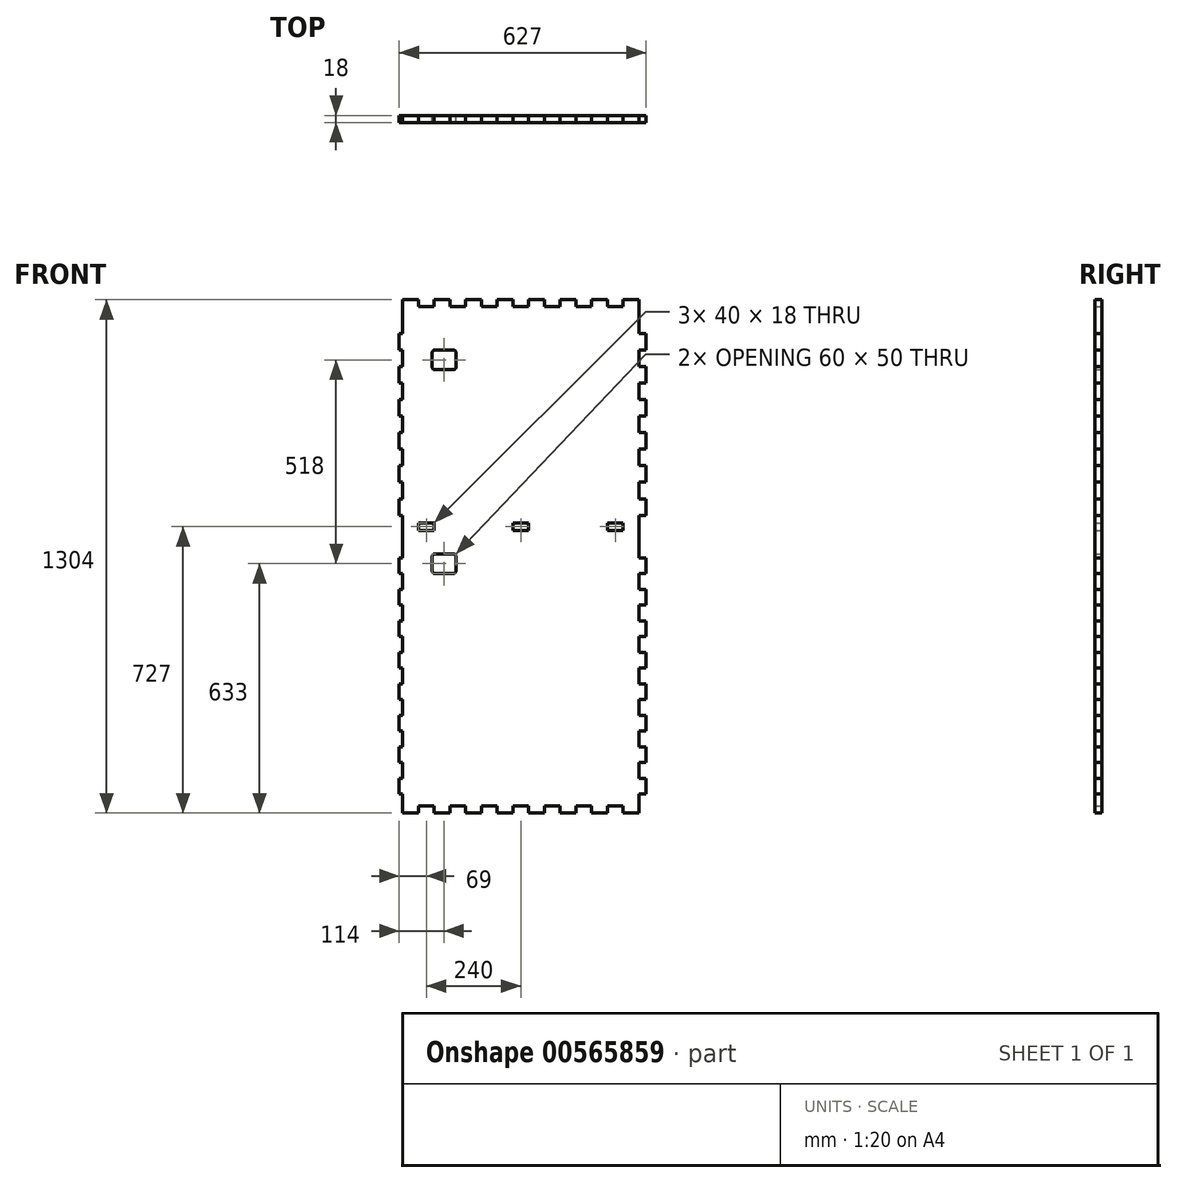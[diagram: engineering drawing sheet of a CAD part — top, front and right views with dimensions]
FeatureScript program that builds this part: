
annotation { "Feature Type Name" : "Feature", "Feature Type Description" : "" }
export const myFeature = defineFeature(function(context is Context, id is Id, definition is map)
    precondition{}
    {
        {
            var Q0;
            Q0=qCreatedBy(makeId("Front.planeOp"),FACE);
            var sketch = newSketch(context, id + "F0", { "sketchPlane" : qUnion([Q0])});
            skLineSegment(sketch, "E0", {"start": v(1332, 1218) * mm, "end": v(1332, 1304) * mm});
            skLineSegment(sketch, "E1", {"start": v(1332, 1304) * mm, "end": v(1292, 1304) * mm});
            skLineSegment(sketch, "E2", {"start": v(1292, 1304) * mm, "end": v(1292, 1286) * mm});
            skLineSegment(sketch, "E3", {"start": v(1292, 1286) * mm, "end": v(1252, 1286) * mm});
            skLineSegment(sketch, "E4", {"start": v(1252, 1304) * mm, "end": v(1252, 1286) * mm});
            skLineSegment(sketch, "E5", {"start": v(1252, 1304) * mm, "end": v(1212, 1304) * mm});
            skLineSegment(sketch, "E6", {"start": v(1212, 1304) * mm, "end": v(1212, 1286) * mm});
            skLineSegment(sketch, "E7", {"start": v(1212, 1286) * mm, "end": v(1172, 1286) * mm});
            skLineSegment(sketch, "E8", {"start": v(1172, 1304) * mm, "end": v(1172, 1286) * mm});
            skLineSegment(sketch, "E9", {"start": v(1172, 1304) * mm, "end": v(1132, 1304) * mm});
            skLineSegment(sketch, "E10", {"start": v(1132, 1304) * mm, "end": v(1132, 1286) * mm});
            skLineSegment(sketch, "E11", {"start": v(1132, 1286) * mm, "end": v(1092, 1286) * mm});
            skLineSegment(sketch, "E12", {"start": v(1092, 1304) * mm, "end": v(1092, 1286) * mm});
            skLineSegment(sketch, "E13", {"start": v(1092, 1304) * mm, "end": v(1052, 1304) * mm});
            skLineSegment(sketch, "E14", {"start": v(1052, 1304) * mm, "end": v(1052, 1286) * mm});
            skLineSegment(sketch, "E15", {"start": v(1052, 1286) * mm, "end": v(1012, 1286) * mm});
            skLineSegment(sketch, "E16", {"start": v(1012, 1304) * mm, "end": v(1012, 1286) * mm});
            skLineSegment(sketch, "E17", {"start": v(1012, 1304) * mm, "end": v(972, 1304) * mm});
            skLineSegment(sketch, "E18", {"start": v(972, 1304) * mm, "end": v(972, 1286) * mm});
            skLineSegment(sketch, "E19", {"start": v(972, 1286) * mm, "end": v(932, 1286) * mm});
            skLineSegment(sketch, "E20", {"start": v(932, 1304) * mm, "end": v(932, 1286) * mm});
            skLineSegment(sketch, "E21", {"start": v(932, 1304) * mm, "end": v(892, 1304) * mm});
            skLineSegment(sketch, "E22", {"start": v(892, 1304) * mm, "end": v(892, 1286) * mm});
            skLineSegment(sketch, "E23", {"start": v(892, 1286) * mm, "end": v(852, 1286) * mm});
            skLineSegment(sketch, "E24", {"start": v(852, 1304) * mm, "end": v(852, 1286) * mm});
            skLineSegment(sketch, "E25", {"start": v(852, 1304) * mm, "end": v(812, 1304) * mm});
            skLineSegment(sketch, "E26", {"start": v(812, 1304) * mm, "end": v(812, 1286) * mm});
            skLineSegment(sketch, "E27", {"start": v(812, 1286) * mm, "end": v(772, 1286) * mm});
            skLineSegment(sketch, "E28", {"start": v(772, 1304) * mm, "end": v(772, 1286) * mm});
            skLineSegment(sketch, "E29", {"start": v(772, 1304) * mm, "end": v(732, 1304) * mm});
            skLineSegment(sketch, "E30", {"start": v(732, 1218) * mm, "end": v(732, 1304) * mm});
            skLineSegment(sketch, "E31", {"start": v(723, 1218) * mm, "end": v(732, 1218) * mm});
            skLineSegment(sketch, "E32", {"start": v(723, 1176) * mm, "end": v(723, 1218) * mm});
            skLineSegment(sketch, "E33", {"start": v(723, 1176) * mm, "end": v(732, 1176) * mm});
            skLineSegment(sketch, "E34", {"start": v(732, 1134) * mm, "end": v(732, 1176) * mm});
            skLineSegment(sketch, "E35", {"start": v(723, 1134) * mm, "end": v(732, 1134) * mm});
            skLineSegment(sketch, "E36", {"start": v(723, 1092) * mm, "end": v(723, 1134) * mm});
            skLineSegment(sketch, "E37", {"start": v(723, 1092) * mm, "end": v(732, 1092) * mm});
            skLineSegment(sketch, "E38", {"start": v(732, 1050) * mm, "end": v(732, 1092) * mm});
            skLineSegment(sketch, "E39", {"start": v(723, 1050) * mm, "end": v(732, 1050) * mm});
            skLineSegment(sketch, "E40", {"start": v(723, 1008) * mm, "end": v(723, 1050) * mm});
            skLineSegment(sketch, "E41", {"start": v(723, 1008) * mm, "end": v(732, 1008) * mm});
            skLineSegment(sketch, "E42", {"start": v(732, 966) * mm, "end": v(732, 1008) * mm});
            skLineSegment(sketch, "E43", {"start": v(723, 966) * mm, "end": v(732, 966) * mm});
            skLineSegment(sketch, "E44", {"start": v(723, 924) * mm, "end": v(723, 966) * mm});
            skLineSegment(sketch, "E45", {"start": v(723, 924) * mm, "end": v(732, 924) * mm});
            skLineSegment(sketch, "E46", {"start": v(732, 882) * mm, "end": v(732, 924) * mm});
            skLineSegment(sketch, "E47", {"start": v(723, 882) * mm, "end": v(732, 882) * mm});
            skLineSegment(sketch, "E48", {"start": v(723, 840) * mm, "end": v(723, 882) * mm});
            skLineSegment(sketch, "E49", {"start": v(723, 840) * mm, "end": v(732, 840) * mm});
            skLineSegment(sketch, "E50", {"start": v(732, 798) * mm, "end": v(732, 840) * mm});
            skLineSegment(sketch, "E51", {"start": v(723, 798) * mm, "end": v(732, 798) * mm});
            skLineSegment(sketch, "E52", {"start": v(723, 756) * mm, "end": v(723, 798) * mm});
            skLineSegment(sketch, "E53", {"start": v(723, 756) * mm, "end": v(732, 756) * mm});
            skLineSegment(sketch, "E54", {"start": v(732, 648) * mm, "end": v(732, 756) * mm});
            skLineSegment(sketch, "E55", {"start": v(723, 648) * mm, "end": v(732, 648) * mm});
            skLineSegment(sketch, "E56", {"start": v(723, 608) * mm, "end": v(723, 648) * mm});
            skLineSegment(sketch, "E57", {"start": v(723, 608) * mm, "end": v(732, 608) * mm});
            skLineSegment(sketch, "E58", {"start": v(732, 568) * mm, "end": v(732, 608) * mm});
            skLineSegment(sketch, "E59", {"start": v(723, 568) * mm, "end": v(732, 568) * mm});
            skLineSegment(sketch, "E60", {"start": v(723, 528) * mm, "end": v(723, 568) * mm});
            skLineSegment(sketch, "E61", {"start": v(723, 528) * mm, "end": v(732, 528) * mm});
            skLineSegment(sketch, "E62", {"start": v(732, 488) * mm, "end": v(732, 528) * mm});
            skLineSegment(sketch, "E63", {"start": v(723, 488) * mm, "end": v(732, 488) * mm});
            skLineSegment(sketch, "E64", {"start": v(723, 448) * mm, "end": v(723, 488) * mm});
            skLineSegment(sketch, "E65", {"start": v(723, 448) * mm, "end": v(732, 448) * mm});
            skLineSegment(sketch, "E66", {"start": v(732, 408) * mm, "end": v(732, 448) * mm});
            skLineSegment(sketch, "E67", {"start": v(723, 408) * mm, "end": v(732, 408) * mm});
            skLineSegment(sketch, "E68", {"start": v(723, 368) * mm, "end": v(723, 408) * mm});
            skLineSegment(sketch, "E69", {"start": v(723, 368) * mm, "end": v(732, 368) * mm});
            skLineSegment(sketch, "E70", {"start": v(732, 328) * mm, "end": v(732, 368) * mm});
            skLineSegment(sketch, "E71", {"start": v(723, 328) * mm, "end": v(732, 328) * mm});
            skLineSegment(sketch, "E72", {"start": v(723, 288) * mm, "end": v(723, 328) * mm});
            skLineSegment(sketch, "E73", {"start": v(723, 288) * mm, "end": v(732, 288) * mm});
            skLineSegment(sketch, "E74", {"start": v(732, 248) * mm, "end": v(732, 288) * mm});
            skLineSegment(sketch, "E75", {"start": v(723, 248) * mm, "end": v(732, 248) * mm});
            skLineSegment(sketch, "E76", {"start": v(723, 208) * mm, "end": v(723, 248) * mm});
            skLineSegment(sketch, "E77", {"start": v(723, 208) * mm, "end": v(732, 208) * mm});
            skLineSegment(sketch, "E78", {"start": v(732, 168) * mm, "end": v(732, 208) * mm});
            skLineSegment(sketch, "E79", {"start": v(723, 168) * mm, "end": v(732, 168) * mm});
            skLineSegment(sketch, "E80", {"start": v(723, 128) * mm, "end": v(723, 168) * mm});
            skLineSegment(sketch, "E81", {"start": v(723, 128) * mm, "end": v(732, 128) * mm});
            skLineSegment(sketch, "E82", {"start": v(732, 88) * mm, "end": v(732, 128) * mm});
            skLineSegment(sketch, "E83", {"start": v(723, 88) * mm, "end": v(732, 88) * mm});
            skLineSegment(sketch, "E84", {"start": v(723, 48) * mm, "end": v(723, 88) * mm});
            skLineSegment(sketch, "E85", {"start": v(723, 48) * mm, "end": v(732, 48) * mm});
            skLineSegment(sketch, "E86", {"start": v(732, 0) * mm, "end": v(732, 48) * mm});
            skLineSegment(sketch, "E87", {"start": v(772, 0) * mm, "end": v(732, 0) * mm});
            skLineSegment(sketch, "E88", {"start": v(772, 18) * mm, "end": v(772, 0) * mm});
            skLineSegment(sketch, "E89", {"start": v(812, 18) * mm, "end": v(772, 18) * mm});
            skLineSegment(sketch, "E90", {"start": v(812, 18) * mm, "end": v(812, 0) * mm});
            skLineSegment(sketch, "E91", {"start": v(852, 0) * mm, "end": v(812, 0) * mm});
            skLineSegment(sketch, "E92", {"start": v(852, 18) * mm, "end": v(852, 0) * mm});
            skLineSegment(sketch, "E93", {"start": v(892, 18) * mm, "end": v(852, 18) * mm});
            skLineSegment(sketch, "E94", {"start": v(892, 18) * mm, "end": v(892, 0) * mm});
            skLineSegment(sketch, "E95", {"start": v(932, 0) * mm, "end": v(892, 0) * mm});
            skLineSegment(sketch, "E96", {"start": v(932, 18) * mm, "end": v(932, 0) * mm});
            skLineSegment(sketch, "E97", {"start": v(972, 18) * mm, "end": v(932, 18) * mm});
            skLineSegment(sketch, "E98", {"start": v(972, 18) * mm, "end": v(972, 0) * mm});
            skLineSegment(sketch, "E99", {"start": v(1012, 0) * mm, "end": v(972, 0) * mm});
            skLineSegment(sketch, "E100", {"start": v(1012, 18) * mm, "end": v(1012, 0) * mm});
            skLineSegment(sketch, "E101", {"start": v(1052, 18) * mm, "end": v(1012, 18) * mm});
            skLineSegment(sketch, "E102", {"start": v(1052, 18) * mm, "end": v(1052, 0) * mm});
            skLineSegment(sketch, "E103", {"start": v(1092, 0) * mm, "end": v(1052, 0) * mm});
            skLineSegment(sketch, "E104", {"start": v(1092, 18) * mm, "end": v(1092, 0) * mm});
            skLineSegment(sketch, "E105", {"start": v(1132, 18) * mm, "end": v(1092, 18) * mm});
            skLineSegment(sketch, "E106", {"start": v(1132, 18) * mm, "end": v(1132, 0) * mm});
            skLineSegment(sketch, "E107", {"start": v(1172, 0) * mm, "end": v(1132, 0) * mm});
            skLineSegment(sketch, "E108", {"start": v(1172, 18) * mm, "end": v(1172, 0) * mm});
            skLineSegment(sketch, "E109", {"start": v(1212, 18) * mm, "end": v(1172, 18) * mm});
            skLineSegment(sketch, "E110", {"start": v(1212, 18) * mm, "end": v(1212, 0) * mm});
            skLineSegment(sketch, "E111", {"start": v(1252, 0) * mm, "end": v(1212, 0) * mm});
            skLineSegment(sketch, "E112", {"start": v(1252, 18) * mm, "end": v(1252, 0) * mm});
            skLineSegment(sketch, "E113", {"start": v(1292, 18) * mm, "end": v(1252, 18) * mm});
            skLineSegment(sketch, "E114", {"start": v(1292, 18) * mm, "end": v(1292, 0) * mm});
            skLineSegment(sketch, "E115", {"start": v(1332, 0) * mm, "end": v(1292, 0) * mm});
            skLineSegment(sketch, "E116", {"start": v(1332, 0) * mm, "end": v(1332, 48) * mm});
            skLineSegment(sketch, "E117", {"start": v(1332, 48) * mm, "end": v(1350, 48) * mm});
            skLineSegment(sketch, "E118", {"start": v(1350, 48) * mm, "end": v(1350, 88) * mm});
            skLineSegment(sketch, "E119", {"start": v(1332, 88) * mm, "end": v(1350, 88) * mm});
            skLineSegment(sketch, "E120", {"start": v(1332, 88) * mm, "end": v(1332, 128) * mm});
            skLineSegment(sketch, "E121", {"start": v(1332, 128) * mm, "end": v(1350, 128) * mm});
            skLineSegment(sketch, "E122", {"start": v(1350, 128) * mm, "end": v(1350, 168) * mm});
            skLineSegment(sketch, "E123", {"start": v(1332, 168) * mm, "end": v(1350, 168) * mm});
            skLineSegment(sketch, "E124", {"start": v(1332, 168) * mm, "end": v(1332, 208) * mm});
            skLineSegment(sketch, "E125", {"start": v(1332, 208) * mm, "end": v(1350, 208) * mm});
            skLineSegment(sketch, "E126", {"start": v(1350, 208) * mm, "end": v(1350, 248) * mm});
            skLineSegment(sketch, "E127", {"start": v(1332, 248) * mm, "end": v(1350, 248) * mm});
            skLineSegment(sketch, "E128", {"start": v(1332, 248) * mm, "end": v(1332, 288) * mm});
            skLineSegment(sketch, "E129", {"start": v(1332, 288) * mm, "end": v(1350, 288) * mm});
            skLineSegment(sketch, "E130", {"start": v(1350, 288) * mm, "end": v(1350, 328) * mm});
            skLineSegment(sketch, "E131", {"start": v(1332, 328) * mm, "end": v(1350, 328) * mm});
            skLineSegment(sketch, "E132", {"start": v(1332, 328) * mm, "end": v(1332, 368) * mm});
            skLineSegment(sketch, "E133", {"start": v(1332, 368) * mm, "end": v(1350, 368) * mm});
            skLineSegment(sketch, "E134", {"start": v(1350, 368) * mm, "end": v(1350, 408) * mm});
            skLineSegment(sketch, "E135", {"start": v(1332, 408) * mm, "end": v(1350, 408) * mm});
            skLineSegment(sketch, "E136", {"start": v(1332, 408) * mm, "end": v(1332, 448) * mm});
            skLineSegment(sketch, "E137", {"start": v(1332, 448) * mm, "end": v(1350, 448) * mm});
            skLineSegment(sketch, "E138", {"start": v(1350, 448) * mm, "end": v(1350, 488) * mm});
            skLineSegment(sketch, "E139", {"start": v(1332, 488) * mm, "end": v(1350, 488) * mm});
            skLineSegment(sketch, "E140", {"start": v(1332, 488) * mm, "end": v(1332, 528) * mm});
            skLineSegment(sketch, "E141", {"start": v(1332, 528) * mm, "end": v(1350, 528) * mm});
            skLineSegment(sketch, "E142", {"start": v(1350, 528) * mm, "end": v(1350, 568) * mm});
            skLineSegment(sketch, "E143", {"start": v(1332, 568) * mm, "end": v(1350, 568) * mm});
            skLineSegment(sketch, "E144", {"start": v(1332, 568) * mm, "end": v(1332, 608) * mm});
            skLineSegment(sketch, "E145", {"start": v(1332, 608) * mm, "end": v(1350, 608) * mm});
            skLineSegment(sketch, "E146", {"start": v(1350, 608) * mm, "end": v(1350, 648) * mm});
            skLineSegment(sketch, "E147", {"start": v(1332, 648) * mm, "end": v(1350, 648) * mm});
            skLineSegment(sketch, "E148", {"start": v(1332, 648) * mm, "end": v(1332, 756) * mm});
            skLineSegment(sketch, "E149", {"start": v(1332, 756) * mm, "end": v(1350, 756) * mm});
            skLineSegment(sketch, "E150", {"start": v(1350, 756) * mm, "end": v(1350, 798) * mm});
            skLineSegment(sketch, "E151", {"start": v(1332, 798) * mm, "end": v(1350, 798) * mm});
            skLineSegment(sketch, "E152", {"start": v(1332, 798) * mm, "end": v(1332, 840) * mm});
            skLineSegment(sketch, "E153", {"start": v(1332, 840) * mm, "end": v(1350, 840) * mm});
            skLineSegment(sketch, "E154", {"start": v(1350, 840) * mm, "end": v(1350, 882) * mm});
            skLineSegment(sketch, "E155", {"start": v(1332, 882) * mm, "end": v(1350, 882) * mm});
            skLineSegment(sketch, "E156", {"start": v(1332, 882) * mm, "end": v(1332, 924) * mm});
            skLineSegment(sketch, "E157", {"start": v(1332, 924) * mm, "end": v(1350, 924) * mm});
            skLineSegment(sketch, "E158", {"start": v(1350, 924) * mm, "end": v(1350, 966) * mm});
            skLineSegment(sketch, "E159", {"start": v(1332, 966) * mm, "end": v(1350, 966) * mm});
            skLineSegment(sketch, "E160", {"start": v(1332, 966) * mm, "end": v(1332, 1008) * mm});
            skLineSegment(sketch, "E161", {"start": v(1332, 1008) * mm, "end": v(1350, 1008) * mm});
            skLineSegment(sketch, "E162", {"start": v(1350, 1008) * mm, "end": v(1350, 1050) * mm});
            skLineSegment(sketch, "E163", {"start": v(1332, 1050) * mm, "end": v(1350, 1050) * mm});
            skLineSegment(sketch, "E164", {"start": v(1332, 1050) * mm, "end": v(1332, 1092) * mm});
            skLineSegment(sketch, "E165", {"start": v(1332, 1092) * mm, "end": v(1350, 1092) * mm});
            skLineSegment(sketch, "E166", {"start": v(1350, 1092) * mm, "end": v(1350, 1134) * mm});
            skLineSegment(sketch, "E167", {"start": v(1332, 1134) * mm, "end": v(1350, 1134) * mm});
            skLineSegment(sketch, "E168", {"start": v(1332, 1134) * mm, "end": v(1332, 1176) * mm});
            skLineSegment(sketch, "E169", {"start": v(1332, 1176) * mm, "end": v(1350, 1176) * mm});
            skLineSegment(sketch, "E170", {"start": v(1350, 1176) * mm, "end": v(1350, 1218) * mm});
            skLineSegment(sketch, "E171", {"start": v(1332, 1218) * mm, "end": v(1350, 1218) * mm});
            skLineSegment(sketch, "E172", {"start": v(772, 736) * mm, "end": v(772, 718) * mm});
            skLineSegment(sketch, "E173", {"start": v(812, 736) * mm, "end": v(772, 736) * mm});
            skLineSegment(sketch, "E174", {"start": v(812, 736) * mm, "end": v(812, 718) * mm});
            skLineSegment(sketch, "E175", {"start": v(812, 718) * mm, "end": v(772, 718) * mm});
            skLineSegment(sketch, "E176", {"start": v(1252, 736) * mm, "end": v(1252, 718) * mm});
            skLineSegment(sketch, "E177", {"start": v(1292, 736) * mm, "end": v(1252, 736) * mm});
            skLineSegment(sketch, "E178", {"start": v(1292, 736) * mm, "end": v(1292, 718) * mm});
            skLineSegment(sketch, "E179", {"start": v(1292, 718) * mm, "end": v(1252, 718) * mm});
            skLineSegment(sketch, "E180", {"start": v(867, 1170) * mm, "end": v(867, 1132) * mm});
            skArc(sketch, "E181", {"start": v(867, 1132) * mm, "mid": v(865.24, 1127.76) * mm, "end": v(861, 1126) * mm});
            skLineSegment(sketch, "E182", {"start": v(861, 1126) * mm, "end": v(813, 1126) * mm});
            skArc(sketch, "E183", {"start": v(813, 1126) * mm, "mid": v(808.76, 1127.76) * mm, "end": v(807, 1132) * mm});
            skLineSegment(sketch, "E184", {"start": v(807, 1170) * mm, "end": v(807, 1132) * mm});
            skArc(sketch, "E185", {"start": v(807, 1170) * mm, "mid": v(808.76, 1174.24) * mm, "end": v(813, 1176) * mm});
            skLineSegment(sketch, "E186", {"start": v(861, 1176) * mm, "end": v(813, 1176) * mm});
            skArc(sketch, "E187", {"start": v(861, 1176) * mm, "mid": v(865.24, 1174.24) * mm, "end": v(867, 1170) * mm});
            skLineSegment(sketch, "E188", {"start": v(807, 652) * mm, "end": v(807, 614) * mm});
            skArc(sketch, "E189", {"start": v(807, 652) * mm, "mid": v(808.76, 656.24) * mm, "end": v(813, 658) * mm});
            skLineSegment(sketch, "E190", {"start": v(861, 658) * mm, "end": v(813, 658) * mm});
            skArc(sketch, "E191", {"start": v(861, 658) * mm, "mid": v(865.24, 656.24) * mm, "end": v(867, 652) * mm});
            skLineSegment(sketch, "E192", {"start": v(867, 652) * mm, "end": v(867, 614) * mm});
            skArc(sketch, "E193", {"start": v(867, 614) * mm, "mid": v(865.24, 609.76) * mm, "end": v(861, 608) * mm});
            skLineSegment(sketch, "E194", {"start": v(861, 608) * mm, "end": v(813, 608) * mm});
            skArc(sketch, "E195", {"start": v(813, 608) * mm, "mid": v(808.76, 609.76) * mm, "end": v(807, 614) * mm});
            skLineSegment(sketch, "E196", {"start": v(1012, 736) * mm, "end": v(1012, 718) * mm});
            skLineSegment(sketch, "E197", {"start": v(1052, 736) * mm, "end": v(1012, 736) * mm});
            skLineSegment(sketch, "E198", {"start": v(1052, 736) * mm, "end": v(1052, 718) * mm});
            skLineSegment(sketch, "E199", {"start": v(1052, 718) * mm, "end": v(1012, 718) * mm});
            skLineSegment(sketch, "E200", {"start": v(812, 803.12) * mm, "end": v(1252, 803.12) * mm, "construction": true});
            skPoint(sketch, "E201", {"position": v(1032, 803.12) * mm});
            skPoint(sketch, "E202", {"position": v(1032, 736) * mm});
            skSolve(sketch);
        }
        {
            var Q0;
            Q0=makeQuery(id+"F0.imprint","IMPRINT",FACE,{"disambiguationData":[TD([[makeQuery(id+"F0.imprint","IMPRINT",EDGE,{"derivedFrom":sQuery(id+"F0.wireOp",EDGE,"E0")}),1.0]])]});
            extrude(context, id + "F1", {"entities" : qUnion([Q0]), "depth" : 18 * mm, "offsetDistance" : 25 * mm});
        }
    });
